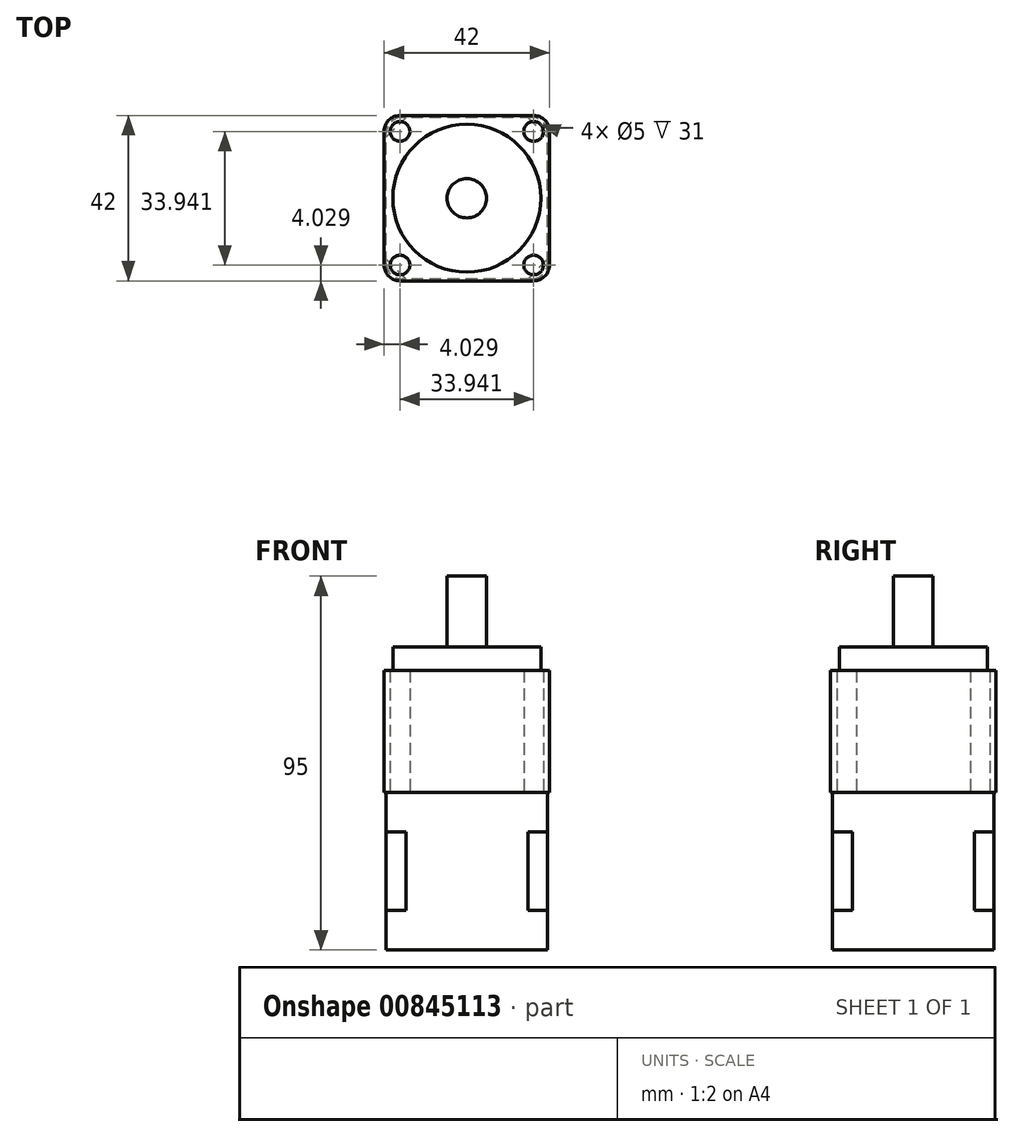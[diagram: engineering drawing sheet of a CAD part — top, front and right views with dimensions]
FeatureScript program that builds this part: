
annotation { "Feature Type Name" : "Feature", "Feature Type Description" : "" }
export const myFeature = defineFeature(function(context is Context, id is Id, definition is map)
    precondition{}
    {
        {
            var Q0;
            Q0=qCreatedBy(makeId("Top.planeOp"),FACE);
            var sketch = newSketch(context, id + "F0", { "sketchPlane" : qUnion([Q0])});
            skLineSegment(sketch, "E0.bottom", {"start": v(21, 21) * mm, "end": v(-21, 21) * mm});
            skLineSegment(sketch, "E0.top", {"start": v(21, -21) * mm, "end": v(-21, -21) * mm});
            skLineSegment(sketch, "E0.left", {"start": v(21, 21) * mm, "end": v(21, -21) * mm});
            skLineSegment(sketch, "E0.right", {"start": v(-21, 21) * mm, "end": v(-21, -21) * mm});
            skPoint(sketch, "E0.middle", {"position": v(0, 0) * mm});
            skCircle(sketch, "E1", {"center": v(0, 0) * mm, "radius": 24 * mm});
            skLineSegment(sketch, "E2", {"start": v(-21, 21) * mm, "end": v(21, -21) * mm});
            skLineSegment(sketch, "E3", {"start": v(-21, -21) * mm, "end": v(21, 21) * mm});
            skCircle(sketch, "E4", {"center": v(-16.97, 16.97) * mm, "radius": 2.5 * mm});
            skCircle(sketch, "E5", {"center": v(16.97, 16.97) * mm, "radius": 2.5 * mm});
            skCircle(sketch, "E6", {"center": v(16.97, -16.97) * mm, "radius": 2.5 * mm});
            skCircle(sketch, "E7", {"center": v(-16.97, -16.97) * mm, "radius": 2.5 * mm});
            skSolve(sketch);
        }
        {
            var Q0;
            {var subQ1=sQuery(id+"F0.wireOp",EDGE,"E0.bottom");var subQ3=sQuery(id+"F0.wireOp",EDGE,"E1");var subQ4=makeQuery(id+"F0.imprint","INTERSECT",VERTEX,{"disambiguationData":[OD(0.0)],"derivedFrom":[subQ1,subQ3]});Q0=makeQuery(id+"F0.imprint","IMPRINT",FACE,{"disambiguationData":[TD([[makeQuery(id+"F0.imprint","IMPRINT",EDGE,{"disambiguationData":[TD([[subQ4,1.0]])],"derivedFrom":subQ3}),-1.0]])]});}
            var Q1;
            {var subQ1=sQuery(id+"F0.wireOp",EDGE,"E0.bottom");var subQ3=sQuery(id+"F0.wireOp",EDGE,"E1");var subQ4=makeQuery(id+"F0.imprint","INTERSECT",VERTEX,{"disambiguationData":[OD(1.0)],"derivedFrom":[subQ1,subQ3]});Q1=makeQuery(id+"F0.imprint","IMPRINT",FACE,{"disambiguationData":[TD([[makeQuery(id+"F0.imprint","IMPRINT",EDGE,{"disambiguationData":[TD([[subQ4,-1.0]])],"derivedFrom":subQ3}),-1.0]])]});}
            var Q2;
            {var subQ1=sQuery(id+"F0.wireOp",EDGE,"E0.top");var subQ3=sQuery(id+"F0.wireOp",EDGE,"E1");var subQ4=makeQuery(id+"F0.imprint","INTERSECT",VERTEX,{"disambiguationData":[OD(0.0)],"derivedFrom":[subQ1,subQ3]});Q2=makeQuery(id+"F0.imprint","IMPRINT",FACE,{"disambiguationData":[TD([[makeQuery(id+"F0.imprint","IMPRINT",EDGE,{"disambiguationData":[TD([[subQ4,-1.0]])],"derivedFrom":subQ3}),-1.0]])]});}
            var Q3;
            {var subQ1=sQuery(id+"F0.wireOp",EDGE,"E0.top");var subQ3=sQuery(id+"F0.wireOp",EDGE,"E1");var subQ4=makeQuery(id+"F0.imprint","INTERSECT",VERTEX,{"disambiguationData":[OD(1.0)],"derivedFrom":[subQ1,subQ3]});Q3=makeQuery(id+"F0.imprint","IMPRINT",FACE,{"disambiguationData":[TD([[makeQuery(id+"F0.imprint","IMPRINT",EDGE,{"disambiguationData":[TD([[subQ4,1.0]])],"derivedFrom":subQ3}),-1.0]])]});}
            var Q4;
            {var subQ1=sQuery(id+"F0.wireOp",EDGE,"E0.left");var subQ3=sQuery(id+"F0.wireOp",EDGE,"E1");var subQ4=makeQuery(id+"F0.imprint","INTERSECT",VERTEX,{"disambiguationData":[OD(0.0)],"derivedFrom":[subQ1,subQ3]});Q4=makeQuery(id+"F0.imprint","IMPRINT",FACE,{"disambiguationData":[TD([[makeQuery(id+"F0.imprint","IMPRINT",EDGE,{"disambiguationData":[TD([[subQ4,-1.0]])],"derivedFrom":subQ3}),-1.0]])]});}
            var Q5;
            {var subQ1=sQuery(id+"F0.wireOp",EDGE,"E0.left");var subQ3=sQuery(id+"F0.wireOp",EDGE,"E1");var subQ4=makeQuery(id+"F0.imprint","INTERSECT",VERTEX,{"disambiguationData":[OD(1.0)],"derivedFrom":[subQ1,subQ3]});Q5=makeQuery(id+"F0.imprint","IMPRINT",FACE,{"disambiguationData":[TD([[makeQuery(id+"F0.imprint","IMPRINT",EDGE,{"disambiguationData":[TD([[subQ4,1.0]])],"derivedFrom":subQ3}),-1.0]])]});}
            var Q6;
            {var subQ1=sQuery(id+"F0.wireOp",EDGE,"E0.right");var subQ3=sQuery(id+"F0.wireOp",EDGE,"E1");var subQ4=makeQuery(id+"F0.imprint","INTERSECT",VERTEX,{"disambiguationData":[OD(0.0)],"derivedFrom":[subQ1,subQ3]});Q6=makeQuery(id+"F0.imprint","IMPRINT",FACE,{"disambiguationData":[TD([[makeQuery(id+"F0.imprint","IMPRINT",EDGE,{"disambiguationData":[TD([[subQ4,1.0]])],"derivedFrom":subQ3}),-1.0]])]});}
            var Q7;
            {var subQ1=sQuery(id+"F0.wireOp",EDGE,"E0.right");var subQ3=sQuery(id+"F0.wireOp",EDGE,"E1");var subQ4=makeQuery(id+"F0.imprint","INTERSECT",VERTEX,{"disambiguationData":[OD(1.0)],"derivedFrom":[subQ1,subQ3]});Q7=makeQuery(id+"F0.imprint","IMPRINT",FACE,{"disambiguationData":[TD([[makeQuery(id+"F0.imprint","IMPRINT",EDGE,{"disambiguationData":[TD([[subQ4,-1.0]])],"derivedFrom":subQ3}),-1.0]])]});}
            var Q8;
            {var subQ0=sQuery(id+"F0.wireOp",EDGE,"E1");var subQ1=sQuery(id+"F0.wireOp",EDGE,"E0.bottom");var subQ9=makeQuery(id+"F0.imprint","INTERSECT",VERTEX,{"disambiguationData":[OD(0.0)],"derivedFrom":[subQ1,subQ0]});Q8=makeQuery(id+"F0.imprint","IMPRINT",FACE,{"disambiguationData":[TD([[makeQuery(id+"F0.imprint","IMPRINT",EDGE,{"disambiguationData":[TD([[subQ9,-1.0]])],"derivedFrom":subQ1}),1.0]])]});}
            var Q9;
            {var subQ5=sQuery(id+"F0.wireOp",EDGE,"E1");var subQ6=sQuery(id+"F0.wireOp",EDGE,"E0.top");var subQ10=makeQuery(id+"F0.imprint","INTERSECT",VERTEX,{"disambiguationData":[OD(0.0)],"derivedFrom":[subQ6,subQ5]});Q9=makeQuery(id+"F0.imprint","IMPRINT",FACE,{"disambiguationData":[TD([[makeQuery(id+"F0.imprint","IMPRINT",EDGE,{"disambiguationData":[TD([[subQ10,-1.0]])],"derivedFrom":subQ6}),-1.0]])]});}
            var Q10;
            {var subQ5=sQuery(id+"F0.wireOp",EDGE,"E1");var subQ6=sQuery(id+"F0.wireOp",EDGE,"E0.left");var subQ9=makeQuery(id+"F0.imprint","INTERSECT",VERTEX,{"disambiguationData":[OD(0.0)],"derivedFrom":[subQ6,subQ5]});Q10=makeQuery(id+"F0.imprint","IMPRINT",FACE,{"disambiguationData":[TD([[makeQuery(id+"F0.imprint","IMPRINT",EDGE,{"disambiguationData":[TD([[subQ9,-1.0]])],"derivedFrom":subQ6}),-1.0]])]});}
            var Q11;
            {var subQ0=sQuery(id+"F0.wireOp",EDGE,"E1");var subQ1=sQuery(id+"F0.wireOp",EDGE,"E0.right");var subQ10=makeQuery(id+"F0.imprint","INTERSECT",VERTEX,{"disambiguationData":[OD(0.0)],"derivedFrom":[subQ1,subQ0]});Q11=makeQuery(id+"F0.imprint","IMPRINT",FACE,{"disambiguationData":[TD([[makeQuery(id+"F0.imprint","IMPRINT",EDGE,{"disambiguationData":[TD([[subQ10,-1.0]])],"derivedFrom":subQ1}),1.0]])]});}
            extrude(context, id + "F1", {"entities" : qUnion([Q0, Q1, Q2, Q3, Q4, Q5, Q6, Q7, Q8, Q9, Q10, Q11]), "depth" : 31 * mm, "offsetDistance" : 25 * mm});
        }
        {
            var Q0;
            Q0=makeQuery(id+"F1.opExtrude","CAP_FACE",FACE,{"disambiguationData":[OSD([sQuery(id+"F0.wireOp",EDGE,"E0.bottom"),sQuery(id+"F0.wireOp",EDGE,"E0.top"),sQuery(id+"F0.wireOp",EDGE,"E0.left"),sQuery(id+"F0.wireOp",EDGE,"E0.right"),sQuery(id+"F0.wireOp",EDGE,"E4"),sQuery(id+"F0.wireOp",EDGE,"E5"),sQuery(id+"F0.wireOp",EDGE,"E6"),sQuery(id+"F0.wireOp",EDGE,"E7")])],"isStart":false});
            var sketch = newSketch(context, id + "F2", { "sketchPlane" : qUnion([Q0])});
            skCircle(sketch, "E8", {"center": v(0, 0) * mm, "radius": 18.8 * mm});
            skSolve(sketch);
        }
        {
            var Q0;
            Q0=makeQuery(id+"F2.imprint","IMPRINT",FACE,{"disambiguationData":[TD([[makeQuery(id+"F2.imprint","IMPRINT",EDGE,{"derivedFrom":sQuery(id+"F2.wireOp",EDGE,"E8")}),1.0]])]});
            extrude(context, id + "F3", {"entities" : qUnion([Q0]), "operationType" : NewBodyOperationType.ADD, "depth" : 6 * mm, "offsetDistance" : 25 * mm});
        }
        {
            var Q0;
            Q0=makeQuery(id+"F3.opExtrude","CAP_FACE",FACE,{"disambiguationData":[OSD([sQuery(id+"F2.wireOp",EDGE,"E8")])],"isStart":false});
            var sketch = newSketch(context, id + "F4", { "sketchPlane" : qUnion([Q0])});
            skCircle(sketch, "E9", {"center": v(0, 0) * mm, "radius": 5 * mm});
            skSolve(sketch);
        }
        {
            var Q0;
            Q0=makeQuery(id+"F4.imprint","IMPRINT",FACE,{"disambiguationData":[TD([[makeQuery(id+"F4.imprint","IMPRINT",EDGE,{"derivedFrom":sQuery(id+"F4.wireOp",EDGE,"E9")}),1.0]])]});
            extrude(context, id + "F5", {"entities" : qUnion([Q0]), "operationType" : NewBodyOperationType.ADD, "depth" : 18 * mm, "offsetDistance" : 25 * mm});
        }
        {
            var Q0;
            Q0=makeQuery(id+"F1.opExtrude","SWEPT_EDGE",EDGE,{"disambiguationData":[OSD([sQuery(id+"F0.wireOp",EDGE,"E0.top"),sQuery(id+"F0.wireOp",EDGE,"E0.right"),sQuery(id+"F0.wireOp",EDGE,"E3")])]});
            var Q1;
            Q1=makeQuery(id+"F1.opExtrude","SWEPT_EDGE",EDGE,{"disambiguationData":[OSD([sQuery(id+"F0.wireOp",EDGE,"E0.bottom"),sQuery(id+"F0.wireOp",EDGE,"E0.right"),sQuery(id+"F0.wireOp",EDGE,"E2")])]});
            var Q2;
            Q2=makeQuery(id+"F1.opExtrude","SWEPT_EDGE",EDGE,{"disambiguationData":[OSD([sQuery(id+"F0.wireOp",EDGE,"E0.bottom"),sQuery(id+"F0.wireOp",EDGE,"E0.left"),sQuery(id+"F0.wireOp",EDGE,"E3")])]});
            var Q3;
            Q3=makeQuery(id+"F1.opExtrude","SWEPT_EDGE",EDGE,{"disambiguationData":[OSD([sQuery(id+"F0.wireOp",EDGE,"E0.top"),sQuery(id+"F0.wireOp",EDGE,"E0.left"),sQuery(id+"F0.wireOp",EDGE,"E2")])]});
            fillet(context, id + "F6", {"entities" : qUnion([Q0, Q1, Q2, Q3]), "radius" : 4 * mm, "tangentPropagation" : true, "allowEdgeOverflow" : false});
        }
        {
            var Q0;
            Q0=makeQuery(id+"F1.opExtrude","CAP_FACE",FACE,{"disambiguationData":[OSD([sQuery(id+"F0.wireOp",EDGE,"E0.bottom"),sQuery(id+"F0.wireOp",EDGE,"E0.top"),sQuery(id+"F0.wireOp",EDGE,"E0.left"),sQuery(id+"F0.wireOp",EDGE,"E0.right"),sQuery(id+"F0.wireOp",EDGE,"E4"),sQuery(id+"F0.wireOp",EDGE,"E5"),sQuery(id+"F0.wireOp",EDGE,"E6"),sQuery(id+"F0.wireOp",EDGE,"E7")])],"isStart":true});
            var sketch = newSketch(context, id + "F7", { "sketchPlane" : qUnion([Q0])});
            skSolve(sketch);
        }
        {
            var Q0;
            {var subQ5=sQuery(id+"F0.wireOp",EDGE,"E4");Q0=makeQuery(id+"F7.imprint","IMPRINT",FACE,{"disambiguationData":[TD([[makeQuery(id+"F7.imprint","IMPRINT",EDGE,{"derivedFrom":makeQuery(id+"F1.opExtrude","CAP_EDGE",EDGE,{"disambiguationData":[OSD([subQ5])],"isStart":true})}),1.0]])]});}
            var sketch = newSketch(context, id + "F8", { "sketchPlane" : qUnion([Q0])});
            skLineSegment(sketch, "E10.bottom", {"start": v(20.5, 20.5) * mm, "end": v(-20.5, 20.5) * mm});
            skLineSegment(sketch, "E10.top", {"start": v(20.5, -20.5) * mm, "end": v(-20.5, -20.5) * mm});
            skLineSegment(sketch, "E10.left", {"start": v(20.5, 20.5) * mm, "end": v(20.5, -20.5) * mm});
            skLineSegment(sketch, "E10.right", {"start": v(-20.5, 20.5) * mm, "end": v(-20.5, -20.5) * mm});
            skPoint(sketch, "E10.middle", {"position": v(0, 0) * mm});
            skSolve(sketch);
        }
        {
            var Q0;
            Q0 = qSketchRegion(id + "F8", true);
            extrude(context, id + "F9", {"entities" : qUnion([Q0]), "operationType" : NewBodyOperationType.ADD, "depth" : 10 * mm, "offsetDistance" : 25 * mm});
        }
        {
            var Q0;
            Q0=makeQuery(id+"F9.opExtrude","SWEPT_EDGE",EDGE,{"disambiguationData":[OSD([sQuery(id+"F8.wireOp",EDGE,"E10.bottom"),sQuery(id+"F8.wireOp",EDGE,"E10.left")])]});
            var Q1;
            Q1=makeQuery(id+"F9.opExtrude","SWEPT_EDGE",EDGE,{"disambiguationData":[OSD([sQuery(id+"F8.wireOp",EDGE,"E10.top"),sQuery(id+"F8.wireOp",EDGE,"E10.left")])]});
            var Q2;
            Q2=makeQuery(id+"F9.opExtrude","SWEPT_EDGE",EDGE,{"disambiguationData":[OSD([sQuery(id+"F8.wireOp",EDGE,"E10.top"),sQuery(id+"F8.wireOp",EDGE,"E10.right")])]});
            var Q3;
            Q3=makeQuery(id+"F9.opExtrude","SWEPT_EDGE",EDGE,{"disambiguationData":[OSD([sQuery(id+"F8.wireOp",EDGE,"E10.bottom"),sQuery(id+"F8.wireOp",EDGE,"E10.right")])]});
            fillet(context, id + "F10", {"entities" : qUnion([Q0, Q1, Q2, Q3]), "radius" : 4 * mm, "tangentPropagation" : true, "allowEdgeOverflow" : false});
        }
        {
            var Q0;
            Q0=makeQuery(id+"F9.opExtrude","CAP_FACE",FACE,{"disambiguationData":[OSD([sQuery(id+"F8.wireOp",EDGE,"E10.bottom"),sQuery(id+"F8.wireOp",EDGE,"E10.top"),sQuery(id+"F8.wireOp",EDGE,"E10.left"),sQuery(id+"F8.wireOp",EDGE,"E10.right")])],"isStart":false});
            var sketch = newSketch(context, id + "F11", { "sketchPlane" : qUnion([Q0])});
            skLineSegment(sketch, "E11.bottom", {"start": v(20.5, -20.5) * mm, "end": v(-20.5, -20.5) * mm});
            skLineSegment(sketch, "E11.top", {"start": v(20.5, 20.5) * mm, "end": v(-20.5, 20.5) * mm});
            skLineSegment(sketch, "E11.left", {"start": v(20.5, -20.5) * mm, "end": v(20.5, 20.5) * mm});
            skLineSegment(sketch, "E11.right", {"start": v(-20.5, -20.5) * mm, "end": v(-20.5, 20.5) * mm});
            skPoint(sketch, "E11.middle", {"position": v(0, 0) * mm});
            skLineSegment(sketch, "E12.bottom", {"start": v(-15.5, 15.5) * mm, "end": v(-25.5, 15.5) * mm});
            skLineSegment(sketch, "E12.top", {"start": v(-15.5, 25.5) * mm, "end": v(-25.5, 25.5) * mm});
            skLineSegment(sketch, "E12.left", {"start": v(-15.5, 15.5) * mm, "end": v(-15.5, 25.5) * mm});
            skLineSegment(sketch, "E12.right", {"start": v(-25.5, 15.5) * mm, "end": v(-25.5, 25.5) * mm});
            skPoint(sketch, "E12.middle", {"position": v(-20.5, 20.5) * mm});
            skLineSegment(sketch, "E13.bottom", {"start": v(25.5, 15.5) * mm, "end": v(15.5, 15.5) * mm});
            skLineSegment(sketch, "E13.top", {"start": v(25.5, 25.5) * mm, "end": v(15.5, 25.5) * mm});
            skLineSegment(sketch, "E13.left", {"start": v(25.5, 15.5) * mm, "end": v(25.5, 25.5) * mm});
            skLineSegment(sketch, "E13.right", {"start": v(15.5, 15.5) * mm, "end": v(15.5, 25.5) * mm});
            skPoint(sketch, "E13.middle", {"position": v(20.5, 20.5) * mm});
            skLineSegment(sketch, "E14.bottom", {"start": v(25.5, -25.5) * mm, "end": v(15.5, -25.5) * mm});
            skLineSegment(sketch, "E14.top", {"start": v(25.5, -15.5) * mm, "end": v(15.5, -15.5) * mm});
            skLineSegment(sketch, "E14.left", {"start": v(25.5, -25.5) * mm, "end": v(25.5, -15.5) * mm});
            skLineSegment(sketch, "E14.right", {"start": v(15.5, -25.5) * mm, "end": v(15.5, -15.5) * mm});
            skPoint(sketch, "E14.middle", {"position": v(20.5, -20.5) * mm});
            skLineSegment(sketch, "E15.bottom", {"start": v(-25.5, -25.5) * mm, "end": v(-15.5, -25.5) * mm});
            skLineSegment(sketch, "E15.top", {"start": v(-25.5, -15.5) * mm, "end": v(-15.5, -15.5) * mm});
            skLineSegment(sketch, "E15.left", {"start": v(-25.5, -25.5) * mm, "end": v(-25.5, -15.5) * mm});
            skLineSegment(sketch, "E15.right", {"start": v(-15.5, -25.5) * mm, "end": v(-15.5, -15.5) * mm});
            skPoint(sketch, "E15.middle", {"position": v(-20.5, -20.5) * mm});
            skLineSegment(sketch, "E16", {"start": v(-15.5, 20.5) * mm, "end": v(-20.5, 15.5) * mm});
            skLineSegment(sketch, "E17", {"start": v(-20.5, -15.5) * mm, "end": v(-15.5, -20.5) * mm});
            skLineSegment(sketch, "E18", {"start": v(15.5, -20.5) * mm, "end": v(20.5, -15.5) * mm});
            skLineSegment(sketch, "E19", {"start": v(20.5, 15.5) * mm, "end": v(15.5, 20.5) * mm});
            skSolve(sketch);
        }
        {
            var Q0;
            {var subQ3=sQuery(id+"F11.wireOp",EDGE,"E16");Q0=makeQuery(id+"F11.imprint","IMPRINT",FACE,{"disambiguationData":[TD([[makeQuery(id+"F11.imprint","IMPRINT",EDGE,{"derivedFrom":subQ3}),1.0]])]});}
            var Q1;
            {var subQ3=sQuery(id+"F11.wireOp",EDGE,"E19");Q1=makeQuery(id+"F11.imprint","IMPRINT",FACE,{"disambiguationData":[TD([[makeQuery(id+"F11.imprint","IMPRINT",EDGE,{"derivedFrom":subQ3}),1.0]])]});}
            var Q2;
            {var subQ3=sQuery(id+"F11.wireOp",EDGE,"E18");Q2=makeQuery(id+"F11.imprint","IMPRINT",FACE,{"disambiguationData":[TD([[makeQuery(id+"F11.imprint","IMPRINT",EDGE,{"derivedFrom":subQ3}),1.0]])]});}
            var Q3;
            {var subQ3=sQuery(id+"F11.wireOp",EDGE,"E17");Q3=makeQuery(id+"F11.imprint","IMPRINT",FACE,{"disambiguationData":[TD([[makeQuery(id+"F11.imprint","IMPRINT",EDGE,{"derivedFrom":subQ3}),1.0]])]});}
            var Q4;
            {var subQ13=sQuery(id+"F11.wireOp",EDGE,"E12.left");var subQ18=sQuery(id+"F11.wireOp",EDGE,"E12.bottom");var subQ19=makeQuery(id+"F11.imprint","INTERSECT",VERTEX,{"derivedFrom":[subQ18,subQ13]});Q4=makeQuery(id+"F11.imprint","IMPRINT",FACE,{"disambiguationData":[TD([[makeQuery(id+"F11.imprint","IMPRINT",EDGE,{"disambiguationData":[TD([[subQ19,-1.0]])],"derivedFrom":subQ18}),1.0]])]});}
            extrude(context, id + "F12", {"entities" : qUnion([Q0, Q1, Q2, Q3, Q4]), "operationType" : NewBodyOperationType.ADD, "depth" : 20 * mm, "offsetDistance" : 25 * mm});
        }
        {
            var Q0;
            Q0=makeQuery(id+"F12.opExtrude","CAP_FACE",FACE,{"disambiguationData":[OSD([sQuery(id+"F11.wireOp",EDGE,"E11.bottom"),sQuery(id+"F11.wireOp",EDGE,"E11.top"),sQuery(id+"F11.wireOp",EDGE,"E11.left"),sQuery(id+"F11.wireOp",EDGE,"E11.right"),sQuery(id+"F11.wireOp",EDGE,"E16"),sQuery(id+"F11.wireOp",EDGE,"E17"),sQuery(id+"F11.wireOp",EDGE,"E18"),sQuery(id+"F11.wireOp",EDGE,"E19")])],"isStart":false});
            var sketch = newSketch(context, id + "F13", { "sketchPlane" : qUnion([Q0])});
            skLineSegment(sketch, "E20.bottom", {"start": v(20.5, -20.5) * mm, "end": v(-20.5, -20.5) * mm});
            skLineSegment(sketch, "E20.top", {"start": v(20.5, 20.5) * mm, "end": v(-20.5, 20.5) * mm});
            skLineSegment(sketch, "E20.left", {"start": v(20.5, -20.5) * mm, "end": v(20.5, 20.5) * mm});
            skLineSegment(sketch, "E20.right", {"start": v(-20.5, -20.5) * mm, "end": v(-20.5, 20.5) * mm});
            skPoint(sketch, "E20.middle", {"position": v(0, 0) * mm});
            skSolve(sketch);
        }
        {
            var Q0;
            Q0 = qSketchRegion(id + "F13", true);
            extrude(context, id + "F14", {"entities" : qUnion([Q0]), "operationType" : NewBodyOperationType.ADD, "depth" : 10 * mm, "offsetDistance" : 25 * mm});
        }
        {
            var Q0;
            Q0=makeQuery(id+"F14.opExtrude","SWEPT_EDGE",EDGE,{"disambiguationData":[OSD([sQuery(id+"F13.wireOp",EDGE,"E20.top"),sQuery(id+"F13.wireOp",EDGE,"E20.left")])]});
            var Q1;
            Q1=makeQuery(id+"F14.opExtrude","SWEPT_EDGE",EDGE,{"disambiguationData":[OSD([sQuery(id+"F13.wireOp",EDGE,"E20.top"),sQuery(id+"F13.wireOp",EDGE,"E20.right")])]});
            var Q2;
            Q2=makeQuery(id+"F14.opExtrude","SWEPT_EDGE",EDGE,{"disambiguationData":[OSD([sQuery(id+"F13.wireOp",EDGE,"E20.bottom"),sQuery(id+"F13.wireOp",EDGE,"E20.left")])]});
            var Q3;
            Q3=makeQuery(id+"F14.opExtrude","SWEPT_EDGE",EDGE,{"disambiguationData":[OSD([sQuery(id+"F13.wireOp",EDGE,"E20.bottom"),sQuery(id+"F13.wireOp",EDGE,"E20.right")])]});
            fillet(context, id + "F15", {"entities" : qUnion([Q0, Q1, Q2, Q3]), "radius" : 4 * mm, "tangentPropagation" : true, "allowEdgeOverflow" : false});
        }
    });
